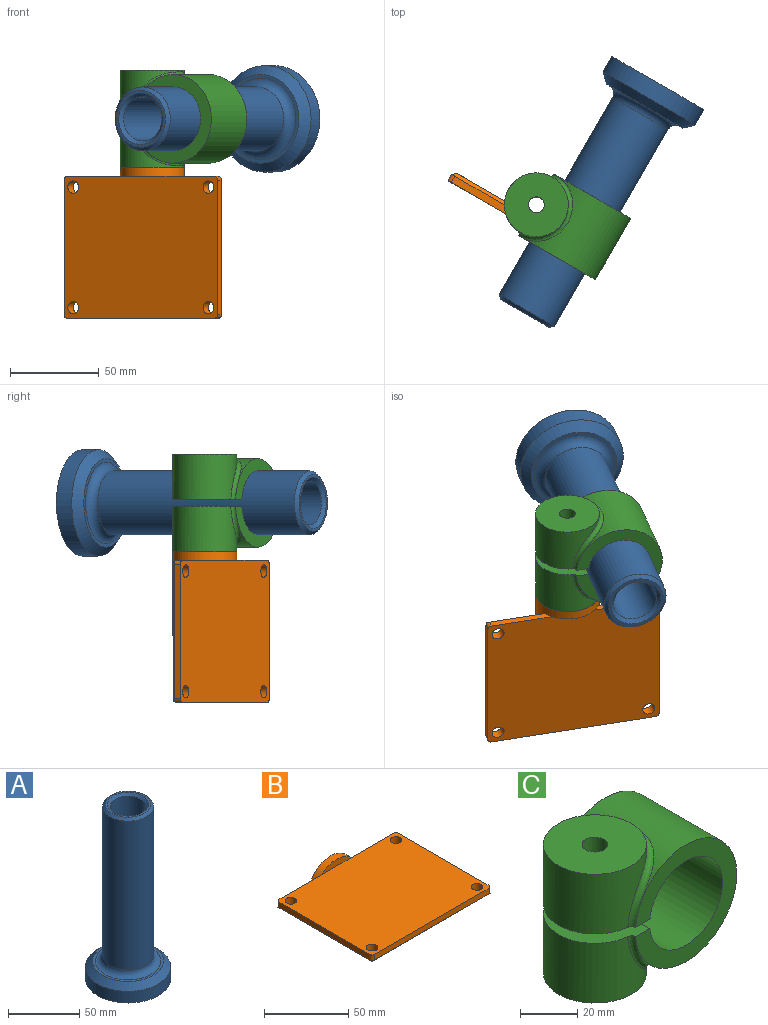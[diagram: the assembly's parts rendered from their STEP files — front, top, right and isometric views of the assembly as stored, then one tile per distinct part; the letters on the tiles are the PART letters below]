
ASSEMBLY  parts=3 mates=2
PART A: 12 faces, bbox 60x60x150 mm
  f0: cylinder r=4.5mm len=65mm, axis (0,0,-1), area 1837.8mm2, adj f3,f8
  f1: cylinder r=30mm len=60mm, axis (0,0,-1), area 1885mm2, adj f3,f4
  f2: plane 50x50mm, normal (0,0,1), area 301.6mm2, adj f4,f7
  f3: plane 60x60mm, normal (0,0,-1), area 2763.8mm2, adj f0,f1
  f4: cone r=25mm half-angle=45deg, axis (0,0,-1), area 1221.8mm2, adj f1,f2
  f5: cylinder r=18mm len=128mm, axis (0,0,-1), area 14476.5mm2, adj f7,f11
  f6: plane 32x32mm, normal (0,0,1), area 143.7mm2, adj f10,f11
  f7: torus R=23mm, axis (0,0,1), area 977.9mm2, adj f2,f5
  f8: plane 25x25mm, normal (0,0,1), area 427.3mm2, adj f0,f9
  f9: cylinder r=12.5mm len=83mm, axis (0,0,1), area 6518.8mm2, adj f8,f10
  f10: cone r=12.5mm half-angle=45deg, axis (0,0,1), area 239.9mm2, adj f6,f9
  f11: cone r=16mm half-angle=45deg, axis (0,0,-1), area 302.1mm2, adj f5,f6
PART B: 33 faces, bbox 100x85x37.5 mm
  f0: cylinder r=18mm len=47mm, axis (0,1,0), area 3548.9mm2, adj f3,f11,f13,f17,f18,f19,f20,f21
  f1: plane 30x22mm, normal (0,-1,0), area 409.2mm2, adj f4,f5,f6,f7,f8,f9,f13,f19
  f2: cylinder r=4.5mm len=12mm, axis (0,1,0), area 339.3mm2, adj f3,f10
  f3: plane 36x36mm, normal (0,1,0), area 954.3mm2, adj f0,f2
  f4: plane 38x6.5mm, normal (-0.87,0,-0.5), area 285.2mm2, adj f1,f5,f9,f10
  f5: plane 38x7.51mm, normal (0,0,-1), area 285.2mm2, adj f1,f4,f6,f10
  f6: plane 38x6.5mm, normal (0.87,0,-0.5), area 285.2mm2, adj f1,f5,f7,f10
  f7: plane 38x6.5mm, normal (0.87,0,0.5), area 285.2mm2, adj f1,f6,f8,f10
  f8: plane 38x7.51mm, normal (0,0,1), area 285.2mm2, adj f1,f7,f9,f10
  f9: plane 38x6.5mm, normal (-0.87,0,0.5), area 285.2mm2, adj f1,f4,f8,f10
  f10: plane 15.01x13mm, normal (0,-1,0), area 82.7mm2, adj f2,f4,f5,f6,f7,f8,f9
  f11: plane 35.55x4mm, normal (0,1,0), area 135.3mm2, adj f0,f12,f21,f29
  f12: plane 100x80mm, normal (0,0,1), area 7842.6mm2, adj f11,f14,f15,f16,f17,f18,f25,f26
  f13: plane 96x76mm, normal (0,0,-1), area 5720.1mm2, adj f0,f1,f19,f20,f21,f22,f23,f24
  f14: plane 76x4mm, normal (-1,0,0), area 304mm2, adj f12,f22,f30,f32
  f15: plane 76x4mm, normal (1,0,0), area 304mm2, adj f12,f23,f29,f31
  f16: plane 96x4mm, normal (0,-1,0), area 384mm2, adj f12,f24,f31,f32
  f17: plane 35.55x4mm, normal (0,1,0), area 135.3mm2, adj f0,f12,f20,f30
  f18: plane 24.9x5mm, normal (0,-1,0), area 85.6mm2, adj f0,f12
  f19: torus R=15mm, axis (0,-1,0), area 318.4mm2, adj f0,f1,f13
  f20: plane 33.86x2.03mm, normal (0,0.71,-0.71), area 92.4mm2, adj f0,f13,f17,f22,f30
  f21: plane 33.86x2.03mm, normal (0,0.71,-0.71), area 92.4mm2, adj f0,f11,f13,f23,f29
  f22: plane 78.83x2mm, normal (-0.71,0,-0.71), area 219.4mm2, adj f13,f14,f20,f24,f30,f32
  f23: plane 78.83x2mm, normal (0.71,0,-0.71), area 219.4mm2, adj f13,f15,f21,f24,f29,f31
  f24: plane 98.83x2mm, normal (0,-0.71,-0.71), area 276mm2, adj f13,f16,f22,f23,f31,f32
  f25: cylinder r=3.5mm len=7mm, axis (0,0,1), area 131.9mm2, adj f12,f13
  f26: cylinder r=3.5mm len=7mm, axis (0,0,1), area 131.9mm2, adj f12,f13
  f27: cylinder r=3.5mm len=7mm, axis (0,0,1), area 131.9mm2, adj f12,f13
  f28: cylinder r=3.5mm len=7mm, axis (0,0,1), area 131.9mm2, adj f12,f13
  f29: cylinder r=2mm len=4.59mm, axis (0,0,1), area 13.2mm2, adj f11,f12,f15,f21,f23
  f30: cylinder r=2mm len=4.59mm, axis (0,0,-1), area 13.2mm2, adj f12,f14,f17,f20,f22
  f31: cylinder r=2mm len=4.59mm, axis (0,0,-1), area 13.2mm2, adj f12,f15,f16,f23,f24
  f32: cylinder r=2mm len=4.59mm, axis (0,0,1), area 13.2mm2, adj f12,f14,f16,f22,f24
PART C: 18 faces, bbox 68.1x40.1x55.1 mm
  f0: cylinder r=25mm len=7.44mm, axis (0,1,0), area 0.4mm2, adj f2,f5,f17
  f1: cylinder r=25mm len=7.44mm, axis (0,1,0), area 0.4mm2, adj f5,f9,f17
  f2: plane 50x49.92mm, normal (0,1,0), area 917.6mm2, adj f0,f6,f7,f14,f16,f17
  f3: cylinder r=18mm len=36mm, axis (0,0,-1), area 1686.8mm2, adj f5,f11,f17
  f4: cylinder r=4.5mm len=25.5mm, axis (0,0,1), area 721mm2, adj f11,f17
  f5: bspline ~39.99x24.68mm, area 296.3mm2, adj f0,f1,f3,f6,f17
  f6: cylinder r=25mm len=50mm, axis (0,1,0), area 3860.7mm2, adj f2,f5,f9,f15
  f7: cylinder r=25mm len=7.44mm, axis (0,1,0), area 0.4mm2, adj f2,f15,f16
  f8: cylinder r=25mm len=7.44mm, axis (0,1,0), area 0.4mm2, adj f9,f15,f16
  f9: plane 50x49.92mm, normal (0,-1,0), area 917.6mm2, adj f1,f6,f8,f14,f16,f17
  f10: cylinder r=18mm len=36mm, axis (0,0,-1), area 1687.3mm2, adj f12,f15,f16
  f11: plane 36x36mm, normal (0,0,1), area 954.3mm2, adj f3,f4
  f12: plane 36x36mm, normal (0,0,-1), area 954.3mm2, adj f10,f13
  f13: cylinder r=4.5mm len=25.5mm, axis (0,0,1), area 721mm2, adj f12,f16
  f14: cylinder r=18mm len=40mm, axis (0,1,0), area 4363.6mm2, adj f2,f9,f16,f17
  f15: bspline ~40x27.48mm, area 296.3mm2, adj f6,f7,f8,f10,f16
  f16: plane 40.07x25.18mm, normal (0,0,1), area 730.9mm2, adj f2,f7,f8,f9,f10,f13,f14,f15
  f17: plane 40.07x25.18mm, normal (0,0,-1), area 730.9mm2, adj f0,f1,f2,f3,f4,f5,f9,f14
PLACE A rot(axis=(0.94,-0.25,-0.25),93.8deg) t=(30.66,20.6,-29.61)mm
PLACE B rot(axis=(0.94,-0.25,-0.25),93.8deg) t=(-37.89,-48.11,-57.11)mm
PLACE C rot(axis=(0,0,-1),30deg) t=(-16.23,-60.61,-29.61)mm
MATE cylindrical A.f5 <-> C.f14  axis (0.5,0.87,0) through (-11.34,-52.15,-29.61)mm
MATE revolute C.f4 <-> B.f0  axis (0,0,-1) through (-37.89,-48.11,-57.11)mm
